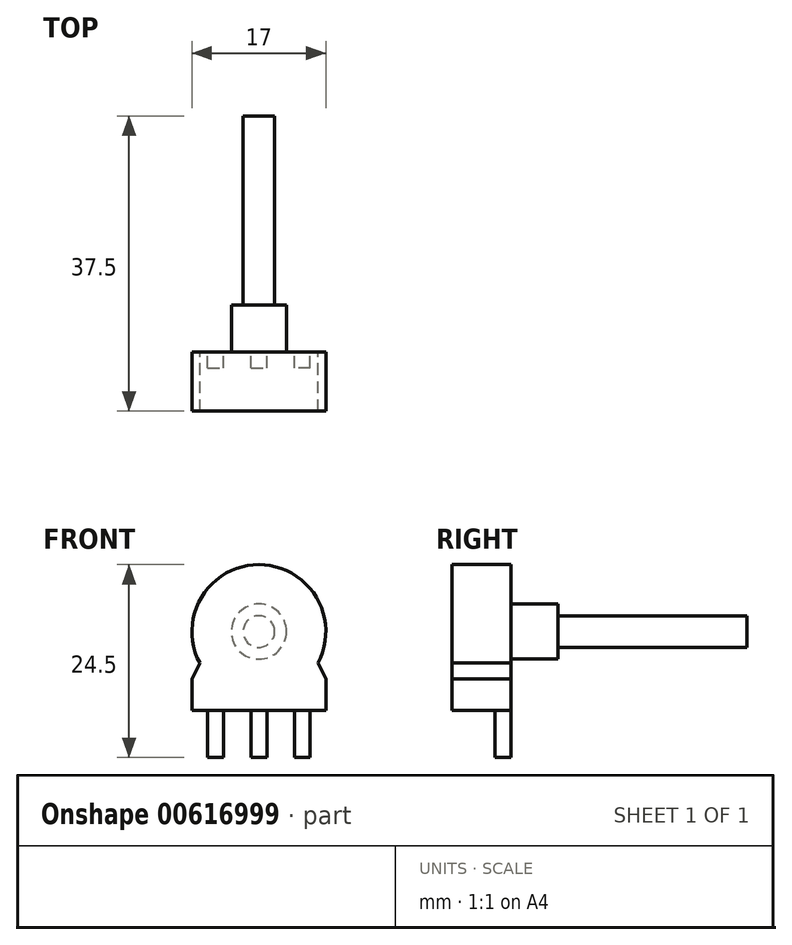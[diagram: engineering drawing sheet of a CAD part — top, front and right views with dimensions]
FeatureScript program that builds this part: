
annotation { "Feature Type Name" : "Feature", "Feature Type Description" : "" }
export const myFeature = defineFeature(function(context is Context, id is Id, definition is map)
    precondition{}
    {
        {
            var Q0;
            Q0=qCreatedBy(makeId("Front.planeOp"),FACE);
            var sketch = newSketch(context, id + "F0", { "sketchPlane" : qUnion([Q0])});
            skArc(sketch, "E0", {"start": v(7.5, -4) * mm, "mid": v(0, 8.5) * mm, "end": v(-7.5, -4) * mm});
            skLineSegment(sketch, "E1", {"start": v(-7.5, -4) * mm, "end": v(7.5, -4) * mm});
            skLineSegment(sketch, "E2", {"start": v(-8.5, 0) * mm, "end": v(-8.5, -10) * mm, "construction": true});
            skLineSegment(sketch, "E3", {"start": v(-7.5, -4) * mm, "end": v(-8.5, -6) * mm});
            skLineSegment(sketch, "E4", {"start": v(-8.5, -6) * mm, "end": v(-8.5, -10) * mm});
            skLineSegment(sketch, "E5", {"start": v(-8.5, -10) * mm, "end": v(0, -10) * mm});
            skLineSegment(sketch, "E6.MirrorCS", {"start": v(8.5, -10) * mm, "end": v(0, -10) * mm});
            skLineSegment(sketch, "E7.MirrorCS", {"start": v(7.5, -4) * mm, "end": v(8.5, -6) * mm});
            skLineSegment(sketch, "E8.MirrorCS", {"start": v(8.5, -6) * mm, "end": v(8.5, -10) * mm});
            skLineSegment(sketch, "E9", {"start": v(-1, -10) * mm, "end": v(-1, -16) * mm});
            skLineSegment(sketch, "E10", {"start": v(-6.5, -10) * mm, "end": v(-6.5, -16) * mm});
            skLineSegment(sketch, "E11", {"start": v(-6.5, -16) * mm, "end": v(-4.5, -16) * mm});
            skLineSegment(sketch, "E12", {"start": v(-4.5, -16) * mm, "end": v(-4.5, -10) * mm});
            skLineSegment(sketch, "E13.MirrorCS", {"start": v(1, -10) * mm, "end": v(1, -16) * mm});
            skLineSegment(sketch, "E14.MirrorCS", {"start": v(4.5, -16) * mm, "end": v(4.5, -10) * mm});
            skLineSegment(sketch, "E15.MirrorCS", {"start": v(6.5, -10) * mm, "end": v(6.5, -16) * mm});
            skLineSegment(sketch, "E16.MirrorCS", {"start": v(6.5, -16) * mm, "end": v(4.5, -16) * mm});
            skPoint(sketch, "E17.end.orphan", {"position": v(0, -13.7) * mm});
            skPoint(sketch, "E18.MirrorCS.start.orphan", {"position": v(1, -16) * mm});
            skLineSegment(sketch, "E19", {"start": v(-1, -16) * mm, "end": v(1, -16) * mm});
            skSolve(sketch);
        }
        {
            var Q0;
            Q0=makeQuery(id+"F0.imprint","IMPRINT",FACE,{"disambiguationData":[TD([[makeQuery(id+"F0.imprint","IMPRINT",EDGE,{"derivedFrom":sQuery(id+"F0.wireOp",EDGE,"E0")}),1.0]])]});
            var Q1;
            Q1=makeQuery(id+"F0.imprint","IMPRINT",FACE,{"disambiguationData":[TD([[makeQuery(id+"F0.imprint","IMPRINT",EDGE,{"derivedFrom":sQuery(id+"F0.wireOp",EDGE,"E1")}),-1.0]])]});
            extrude(context, id + "F1", {"entities" : qUnion([Q0, Q1]), "depth" : 7.5 * mm, "offsetDistance" : 25 * mm});
        }
        {
            var Q0;
            {var subQ0=sQuery(id+"F0.wireOp",EDGE,"E10");Q0=makeQuery(id+"F0.imprint","IMPRINT",FACE,{"disambiguationData":[TD([[makeQuery(id+"F0.imprint","IMPRINT",EDGE,{"derivedFrom":subQ0}),1.0]])]});}
            var Q1;
            {var subQ4=sQuery(id+"F0.wireOp",EDGE,"E9");Q1=makeQuery(id+"F0.imprint","IMPRINT",FACE,{"disambiguationData":[TD([[makeQuery(id+"F0.imprint","IMPRINT",EDGE,{"derivedFrom":subQ4}),1.0]])]});}
            var Q2;
            {var subQ0=sQuery(id+"F0.wireOp",EDGE,"E14.MirrorCS");Q2=makeQuery(id+"F0.imprint","IMPRINT",FACE,{"disambiguationData":[TD([[makeQuery(id+"F0.imprint","IMPRINT",EDGE,{"derivedFrom":subQ0}),-1.0]])]});}
            extrude(context, id + "F2", {"entities" : qUnion([Q0, Q1, Q2]), "operationType" : NewBodyOperationType.ADD, "depth" : 2 * mm, "offsetDistance" : 25 * mm});
        }
        {
            var Q0;
            Q0=makeQuery(id+"F0.imprint","IMPRINT",FACE,{"disambiguationData":[TD([[makeQuery(id+"F0.imprint","IMPRINT",EDGE,{"derivedFrom":sQuery(id+"F0.wireOp",EDGE,"E0")}),1.0]])]});
            var sketch = newSketch(context, id + "F3", { "sketchPlane" : qUnion([Q0])});
            skCircle(sketch, "E20", {"center": v(0, 0) * mm, "radius": 3.5 * mm});
            skSolve(sketch);
        }
        {
            var Q0;
            Q0=makeQuery(id+"F3.imprint","IMPRINT",FACE,{"disambiguationData":[TD([[makeQuery(id+"F3.imprint","IMPRINT",EDGE,{"derivedFrom":sQuery(id+"F3.wireOp",EDGE,"E20")}),1.0]])]});
            extrude(context, id + "F4", {"entities" : qUnion([Q0]), "operationType" : NewBodyOperationType.ADD, "oppositeDirection" : true, "depth" : 6 * mm, "offsetDistance" : 25 * mm});
        }
        {
            var Q0;
            Q0=makeQuery(id+"F4.opExtrude","CAP_FACE",FACE,{"disambiguationData":[OSD([sQuery(id+"F3.wireOp",EDGE,"E20")])],"isStart":false});
            var sketch = newSketch(context, id + "F5", { "sketchPlane" : qUnion([Q0])});
            skCircle(sketch, "E21", {"center": v(0, 0) * mm, "radius": 2 * mm});
            skSolve(sketch);
        }
        {
            var Q0;
            Q0 = qSketchRegion(id + "F5", true);
            extrude(context, id + "F6", {"entities" : qUnion([Q0]), "operationType" : NewBodyOperationType.ADD, "depth" : 24 * mm, "offsetDistance" : 25 * mm});
        }
    });
